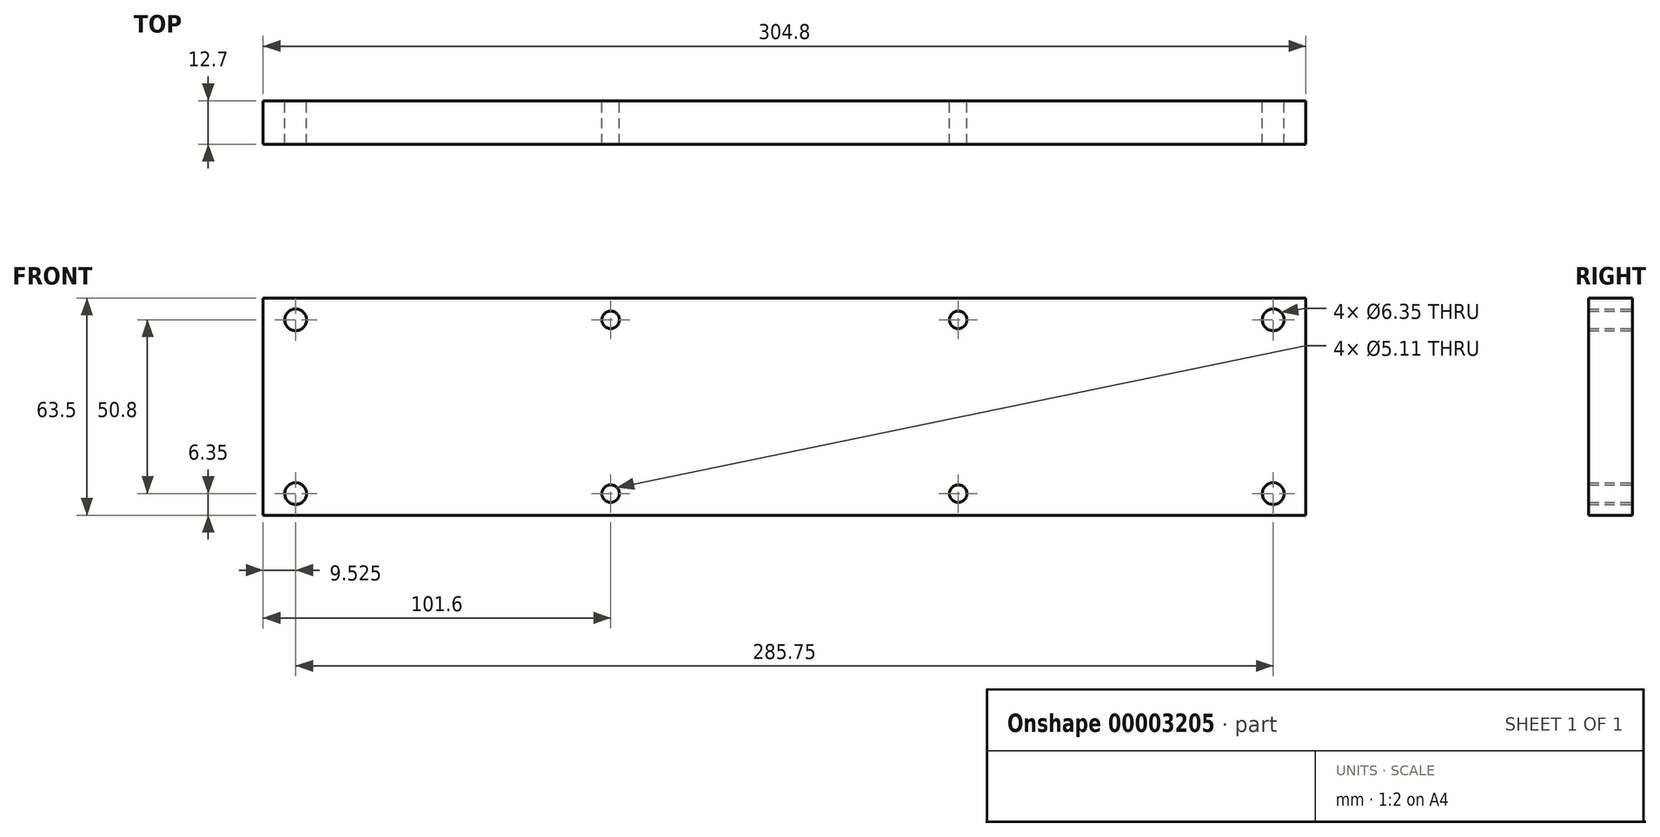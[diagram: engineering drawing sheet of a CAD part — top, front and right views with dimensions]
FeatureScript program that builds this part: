
annotation { "Feature Type Name" : "Feature", "Feature Type Description" : "" }
export const myFeature = defineFeature(function(context is Context, id is Id, definition is map)
    precondition{}
    {
        {
            var Q0;
            Q0=qCreatedBy(makeId("Front.planeOp"),FACE);
            var sketch = newSketch(context, id + "F0", { "sketchPlane" : qUnion([Q0])});
            skLineSegment(sketch, "E0", {"start": v(0, 0) * mm, "end": v(0, -63.5) * mm});
            skLineSegment(sketch, "E1", {"start": v(0, -63.5) * mm, "end": v(304.8, -63.5) * mm});
            skLineSegment(sketch, "E2", {"start": v(304.8, -63.5) * mm, "end": v(304.8, 0) * mm});
            skLineSegment(sketch, "E3", {"start": v(304.8, 0) * mm, "end": v(0, 0) * mm});
            skLineSegment(sketch, "E4", {"start": v(0, -6.35) * mm, "end": v(304.8, -6.35) * mm, "construction": true});
            skLineSegment(sketch, "E5", {"start": v(0, -57.15) * mm, "end": v(304.8, -57.15) * mm, "construction": true});
            skLineSegment(sketch, "E6", {"start": v(9.52, 0) * mm, "end": v(9.53, -63.5) * mm, "construction": true});
            skLineSegment(sketch, "E7", {"start": v(295.28, 0) * mm, "end": v(295.28, -63.5) * mm, "construction": true});
            skLineSegment(sketch, "E8", {"start": v(101.6, 0) * mm, "end": v(101.6, -63.5) * mm, "construction": true});
            skLineSegment(sketch, "E9", {"start": v(203.2, 0) * mm, "end": v(203.2, -63.5) * mm, "construction": true});
            skCircle(sketch, "E10", {"center": v(9.53, -6.35) * mm, "radius": 3.18 * mm});
            skCircle(sketch, "E11", {"center": v(9.53, -57.15) * mm, "radius": 3.18 * mm});
            skCircle(sketch, "E12", {"center": v(101.6, -6.35) * mm, "radius": 2.55 * mm});
            skCircle(sketch, "E13", {"center": v(101.6, -57.15) * mm, "radius": 2.55 * mm});
            skCircle(sketch, "E14", {"center": v(203.2, -6.35) * mm, "radius": 2.55 * mm});
            skCircle(sketch, "E15", {"center": v(203.2, -57.15) * mm, "radius": 2.55 * mm});
            skCircle(sketch, "E16", {"center": v(295.28, -6.35) * mm, "radius": 3.18 * mm});
            skCircle(sketch, "E17", {"center": v(295.28, -57.15) * mm, "radius": 3.18 * mm});
            skSolve(sketch);
        }
        {
            var Q0;
            Q0=makeQuery(id+"F0.imprint","IMPRINT",FACE,{"disambiguationData":[TD([[makeQuery(id+"F0.imprint","IMPRINT",EDGE,{"derivedFrom":sQuery(id+"F0.wireOp",EDGE,"E0")}),1.0]])]});
            extrude(context, id + "F1", {"entities" : qUnion([Q0]), "endBound" : BoundingType.SYMMETRIC, "depth" : 12.7 * mm});
        }
    });
